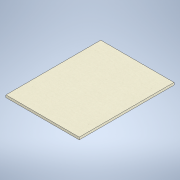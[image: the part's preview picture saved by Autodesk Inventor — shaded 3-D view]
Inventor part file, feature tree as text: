
AUTODESK INVENTOR PART (.ipt)
format: ipt  version: 2021 (Build 250183000, 183)  size: 99,840 bytes
history: native  units: mm
features: extrude x1, sketch x1
ambient origin geometry x8: Origin, YZ Plane, XZ Plane, XY Plane, X Axis, Y Axis, Z Axis, Center Point
bodies: Solid1 (feature_tree)
feature tree (2):
  extrude  "Extrusion1"  Depth=279.4mm
  sketch  "Sketch1"  dims[d0=215.9mm d1=279.4mm d2=7.0mm d3=0.0mm]
